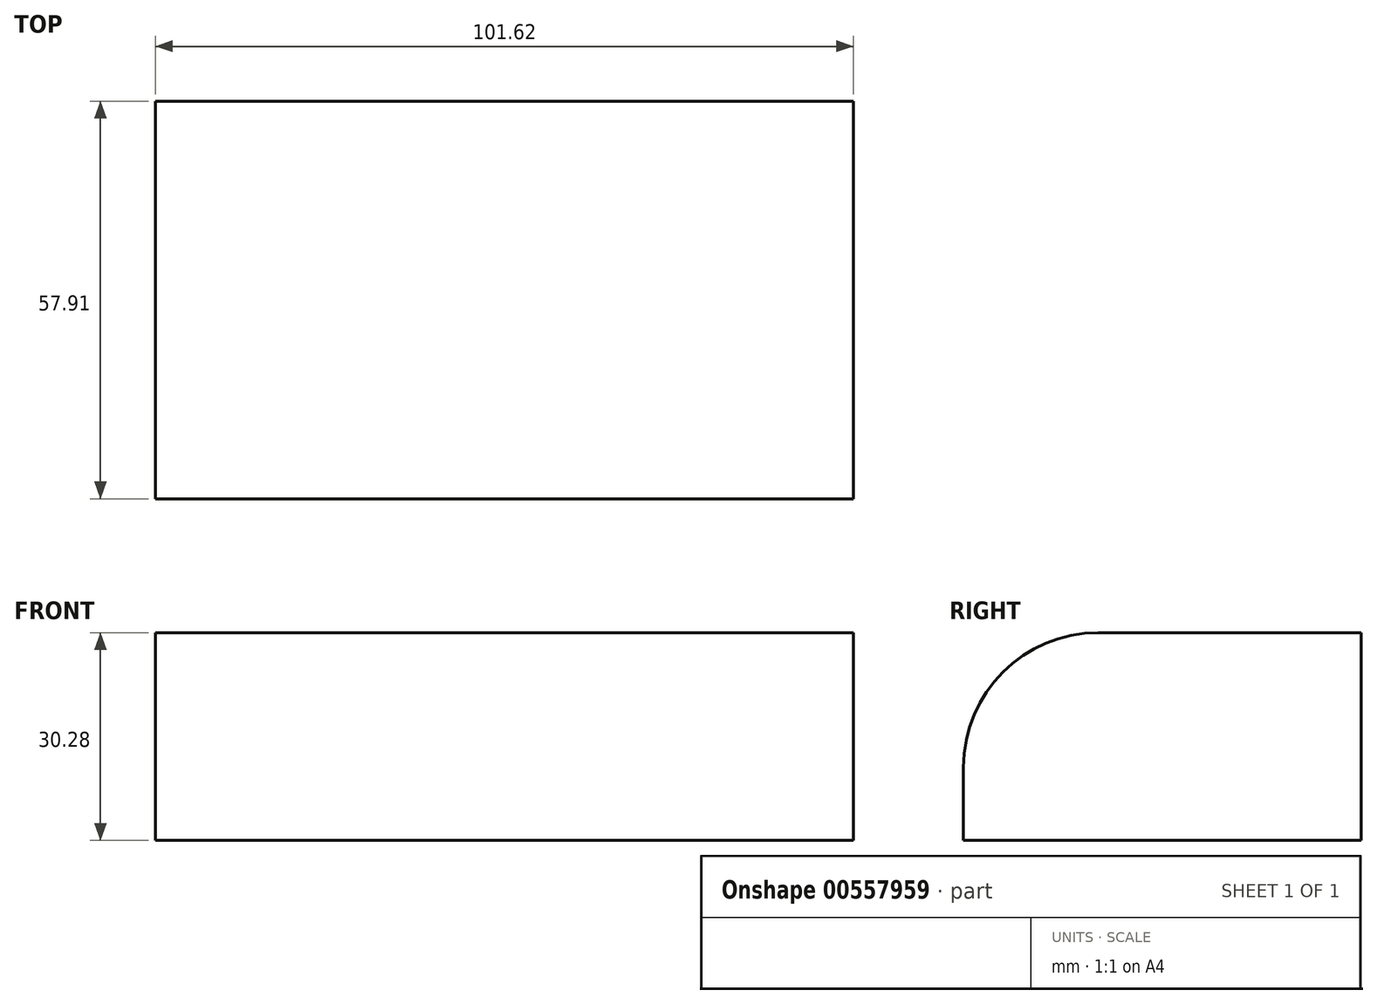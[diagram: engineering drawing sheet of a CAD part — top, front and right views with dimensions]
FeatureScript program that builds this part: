
annotation { "Feature Type Name" : "Feature", "Feature Type Description" : "" }
export const myFeature = defineFeature(function(context is Context, id is Id, definition is map)
    precondition{}
    {
        {
            var Q0;
            Q0=qCreatedBy(makeId("Front.planeOp"),FACE);
            var sketch = newSketch(context, id + "F0", { "sketchPlane" : qUnion([Q0])});
            skLineSegment(sketch, "E0.bottom", {"start": v(50.8, -15.14) * mm, "end": v(-50.8, -15.14) * mm});
            skLineSegment(sketch, "E0.top", {"start": v(50.8, 15.14) * mm, "end": v(-50.8, 15.14) * mm});
            skLineSegment(sketch, "E0.left", {"start": v(50.8, -15.14) * mm, "end": v(50.8, 15.14) * mm});
            skLineSegment(sketch, "E0.right", {"start": v(-50.8, -15.14) * mm, "end": v(-50.8, 15.14) * mm});
            skPoint(sketch, "E0.middle", {"position": v(0, 0) * mm});
            skLineSegment(sketch, "E1.bottom", {"start": v(119.58, 52.6) * mm, "end": v(52.86, 52.6) * mm});
            skLineSegment(sketch, "E1.top", {"start": v(119.58, 112.13) * mm, "end": v(52.86, 112.13) * mm});
            skLineSegment(sketch, "E1.left", {"start": v(119.58, 52.6) * mm, "end": v(119.58, 112.13) * mm});
            skLineSegment(sketch, "E1.right", {"start": v(52.86, 52.6) * mm, "end": v(52.86, 112.13) * mm});
            skPoint(sketch, "E1.middle", {"position": v(86.22, 82.37) * mm});
            skLineSegment(sketch, "E2", {"start": v(50.8, 15.14) * mm, "end": v(50.8, 39.77) * mm});
            skSolve(sketch);
        }
        {
            var Q0;
            Q0=makeQuery(id+"F0.imprint","IMPRINT",FACE,{"disambiguationData":[TD([[makeQuery(id+"F0.imprint","IMPRINT",EDGE,{"derivedFrom":sQuery(id+"F0.wireOp",EDGE,"E0.bottom")}),-1.0]])]});
            extrude(context, id + "F1", {"entities" : qUnion([Q0]), "depth" : 57.9 * mm, "offsetDistance" : 25.4 * mm});
        }
        {
            var Q0;
            Q0=makeQuery(id+"F1.opExtrude","CAP_EDGE",EDGE,{"disambiguationData":[OSD([sQuery(id+"F0.wireOp",EDGE,"E0.top")])],"isStart":false});
            fillet(context, id + "F2", {"entities" : qUnion([Q0]), "radius" : 19.62 * mm, "tangentPropagation" : true, "allowEdgeOverflow" : false});
        }
    });
